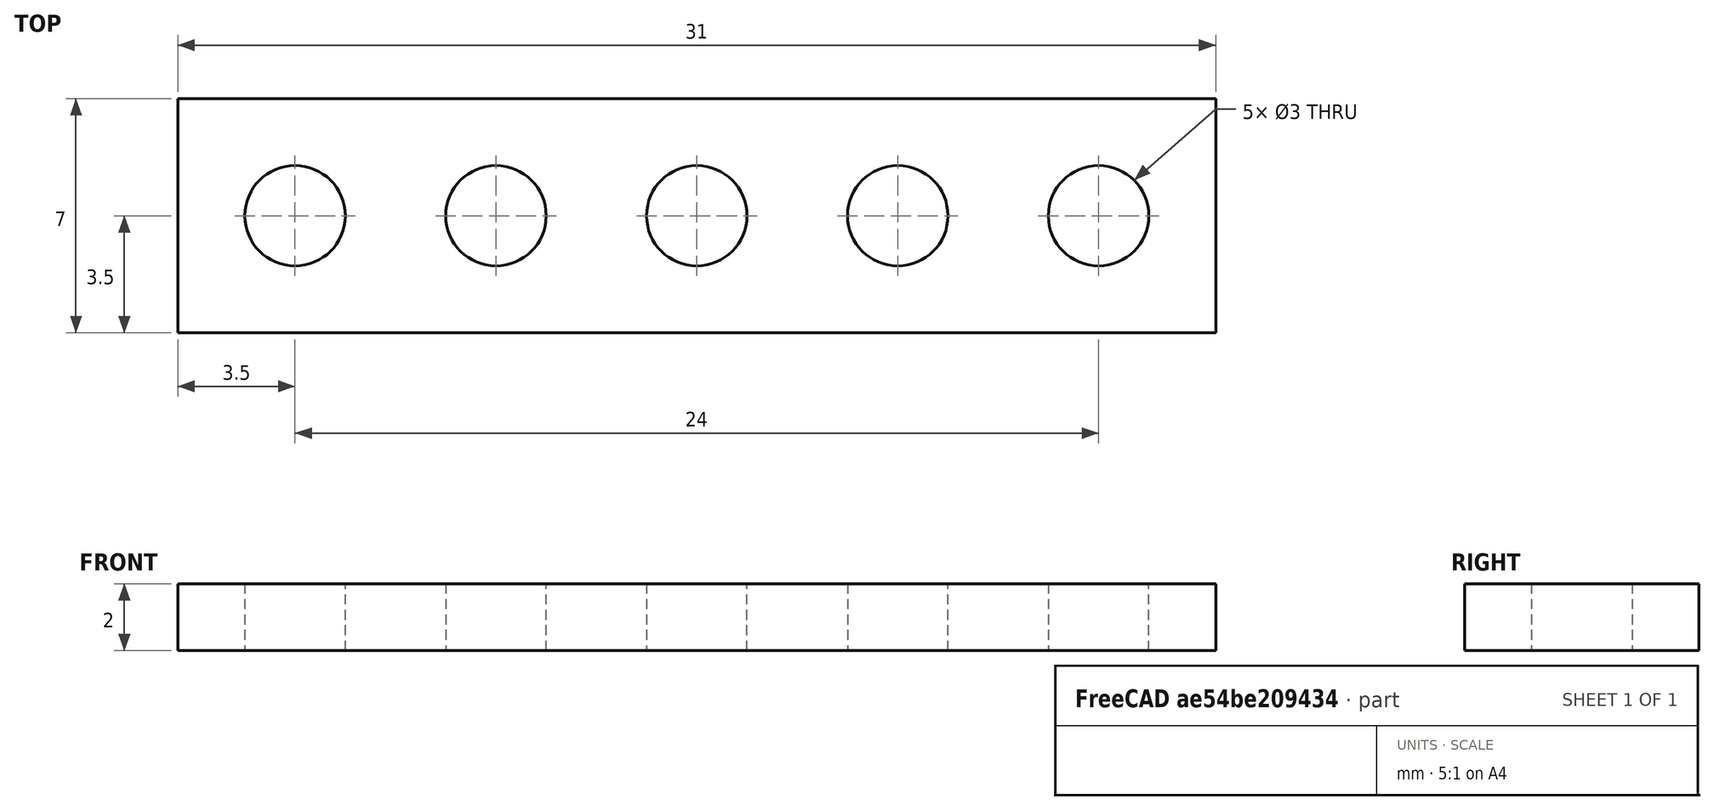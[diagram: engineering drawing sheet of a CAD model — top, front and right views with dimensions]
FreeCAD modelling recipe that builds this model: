
FCSTD DOCUMENT  (FreeCAD 0.21R33694 (Git))
Label: OJT1_T10_R02Taladro
License: All rights reserved
LicenseURL: https://en.wikipedia.org/wiki/All_rights_reserved
objects: Part::Box×1, Part::Cylinder×1, Part::FeaturePython×1, Part::Cut×1
note: 3 computed .brp shape members not serialized (recipe doc carries the construction recipe); baked Part::Feature solids carry a one-line shape summary decoded from their .brp

FEATURE [Part::Box] Box  label="Cub"
  AttacherType = Attacher::AttachEngine3D
  Height = 2
  Length = 31
  Width = 7
FEATURE [Part::Cylinder] Cylinder  label="Cilindre"
  Angle = 360
  AttacherType = Attacher::AttachEngine3D
  FirstAngle = 0
  Height = 2
  Placement = pos=(3.5,3.5,0) rot=(0,0,1;0rad)
  Radius = 1.5
  SecondAngle = 0
  expr: .Placement.Base.x = 3.5
  expr: .Placement.Base.y = 3.5
FEATURE [Part::FeaturePython] Array  # Draft array (typed FeaturePython)
  AlwaysSyncPlacement = false
  Angle = 360
  ArrayType = 0
  Axis = (0,0,1)
  Base = -> Cylinder
  Center = (0,0,0)
  Count = 5
  ExpandArray = false
  Fuse = false
  IntervalAxis = (0,0,0)
  IntervalX = (6,0,0)
  IntervalY = (0,100,0)
  IntervalZ = (0,0,100)
  NumberCircles = 3
  NumberPolar = 5
  NumberX = 5
  NumberY = 0
  NumberZ = 0
  PlacementList = 5 placements: arithmetic series from (3.5,3.5,0) step (6,0,0) to (27.5,3.5,0)
  RadialDistance = 50
  ScaleList = (5) [(1,1,1),(1,1,1),(1,1,1),(1,1,1),(1,1,1)]
  Symmetry = 1
  TangentialDistance = 25
FEATURE [Part::Cut] Cut
  Base = -> Box
  Tool = -> Array
